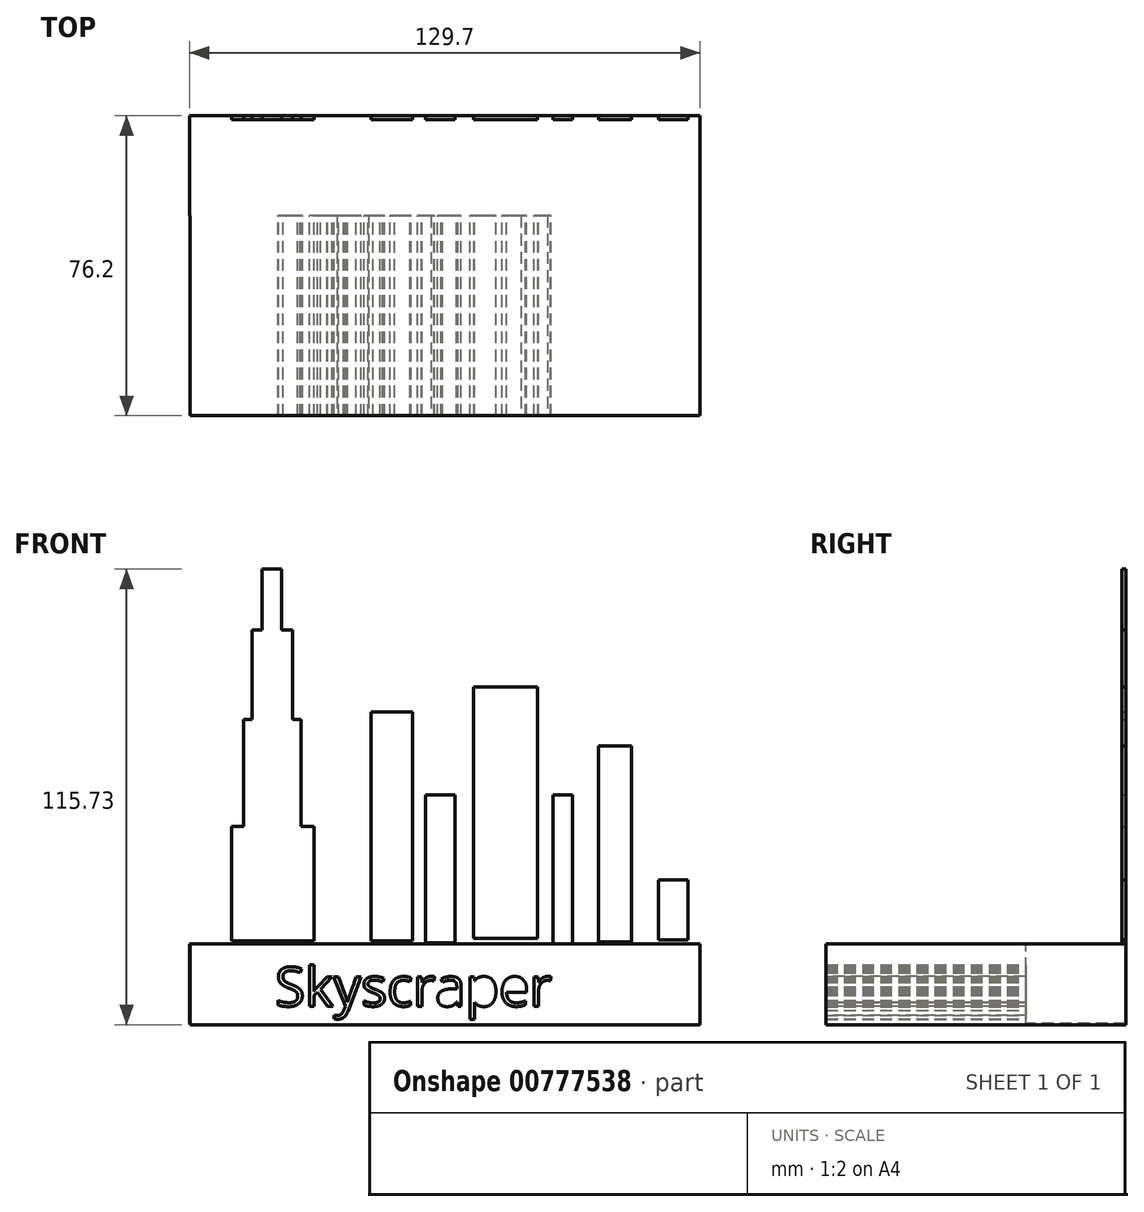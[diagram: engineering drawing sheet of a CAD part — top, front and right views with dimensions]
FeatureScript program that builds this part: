
annotation { "Feature Type Name" : "Feature", "Feature Type Description" : "" }
export const myFeature = defineFeature(function(context is Context, id is Id, definition is map)
    precondition{}
    {
        {
            var Q0;
            Q0=qCreatedBy(makeId("Front.planeOp"),FACE);
            var sketch = newSketch(context, id + "F0", { "sketchPlane" : qUnion([Q0])});
            skLineSegment(sketch, "E0.bottom", {"start": v(-62.22, -50.32) * mm, "end": v(67.34, -50.32) * mm});
            skLineSegment(sketch, "E0.top", {"start": v(-62.22, -29.83) * mm, "end": v(67.34, -29.83) * mm});
            skLineSegment(sketch, "E0.left", {"start": v(-62.22, -50.32) * mm, "end": v(-62.22, -29.83) * mm});
            skLineSegment(sketch, "E0.right", {"start": v(67.34, -50.32) * mm, "end": v(67.34, -29.83) * mm});
            skText(sketch, "E1", { "text": "Skyscraper", "fontName": "OpenSans-Regular.ttf"});
            const initialGuessF0  = {"E1": [-0.04063, -0.04561, 1, 0, 0.00997]};
            skSetInitialGuess(sketch, initialGuessF0);
            skSolve(sketch);
        }
        {
            var Q0;
            Q0=qCreatedBy(makeId("Front.planeOp"),FACE);
            var sketch = newSketch(context, id + "F1", { "sketchPlane" : qUnion([Q0])});
            skLineSegment(sketch, "E2.bottom", {"start": v(-51.7, -29) * mm, "end": v(-30.66, -29) * mm});
            skLineSegment(sketch, "E2.top", {"start": v(-51.7, 0) * mm, "end": v(-30.66, 0) * mm});
            skLineSegment(sketch, "E2.left", {"start": v(-51.7, -29) * mm, "end": v(-51.7, 0) * mm});
            skLineSegment(sketch, "E2.right", {"start": v(-30.66, -29) * mm, "end": v(-30.66, 0) * mm});
            skLineSegment(sketch, "E3.bottom", {"start": v(-48.66, 0) * mm, "end": v(-33.98, 0) * mm});
            skLineSegment(sketch, "E3.top", {"start": v(-48.66, 27.2) * mm, "end": v(-33.98, 27.2) * mm});
            skLineSegment(sketch, "E3.left", {"start": v(-48.66, 0) * mm, "end": v(-48.66, 27.2) * mm});
            skLineSegment(sketch, "E3.right", {"start": v(-33.98, 0) * mm, "end": v(-33.98, 27.2) * mm});
            skLineSegment(sketch, "E4.bottom", {"start": v(-46.44, 27.2) * mm, "end": v(-36.2, 27.2) * mm});
            skLineSegment(sketch, "E4.top", {"start": v(-46.44, 49.9) * mm, "end": v(-36.2, 49.9) * mm});
            skLineSegment(sketch, "E4.left", {"start": v(-46.44, 27.2) * mm, "end": v(-46.44, 49.9) * mm});
            skLineSegment(sketch, "E4.right", {"start": v(-36.2, 27.2) * mm, "end": v(-36.2, 49.9) * mm});
            skLineSegment(sketch, "E5.bottom", {"start": v(-43.95, 49.9) * mm, "end": v(-38.97, 49.9) * mm});
            skLineSegment(sketch, "E5.top", {"start": v(-43.95, 65.4) * mm, "end": v(-38.97, 65.4) * mm});
            skLineSegment(sketch, "E5.left", {"start": v(-43.95, 49.9) * mm, "end": v(-43.95, 65.4) * mm});
            skLineSegment(sketch, "E5.right", {"start": v(-38.97, 49.9) * mm, "end": v(-38.97, 65.4) * mm});
            skPoint(sketch, "E6.oppositeSnap0", {"position": v(-41.46, 65.4) * mm});
            skLineSegment(sketch, "E6.bottom", {"start": v(-41.46, 65.4) * mm, "end": v(-41.46, 65.4) * mm});
            skLineSegment(sketch, "E6.top", {"start": v(-41.46, 73.99) * mm, "end": v(-41.46, 73.99) * mm});
            skLineSegment(sketch, "E6.left", {"start": v(-41.46, 65.4) * mm, "end": v(-41.46, 73.99) * mm});
            skLineSegment(sketch, "E6.right", {"start": v(-41.46, 65.4) * mm, "end": v(-41.46, 73.99) * mm});
            skLineSegment(sketch, "E7.bottom", {"start": v(-16.27, -29) * mm, "end": v(-5.74, -29) * mm});
            skLineSegment(sketch, "E7.top", {"start": v(-16.27, 29.14) * mm, "end": v(-5.74, 29.14) * mm});
            skLineSegment(sketch, "E7.left", {"start": v(-16.27, -29) * mm, "end": v(-16.27, 29.14) * mm});
            skLineSegment(sketch, "E7.right", {"start": v(-5.74, -29) * mm, "end": v(-5.74, 29.14) * mm});
            skLineSegment(sketch, "E8.bottom", {"start": v(9.76, -28.45) * mm, "end": v(26.1, -28.45) * mm});
            skLineSegment(sketch, "E8.top", {"start": v(9.76, 35.5) * mm, "end": v(26.1, 35.5) * mm});
            skLineSegment(sketch, "E8.left", {"start": v(9.76, -28.45) * mm, "end": v(9.76, 35.5) * mm});
            skLineSegment(sketch, "E8.right", {"start": v(26.1, -28.45) * mm, "end": v(26.1, 35.5) * mm});
            skLineSegment(sketch, "E9.bottom", {"start": v(41.6, -29.28) * mm, "end": v(49.9, -29.28) * mm});
            skLineSegment(sketch, "E9.top", {"start": v(41.6, 20.56) * mm, "end": v(49.9, 20.56) * mm});
            skLineSegment(sketch, "E9.left", {"start": v(41.6, -29.28) * mm, "end": v(41.6, 20.56) * mm});
            skLineSegment(sketch, "E9.right", {"start": v(49.9, -29.28) * mm, "end": v(49.9, 20.56) * mm});
            skLineSegment(sketch, "E10.bottom", {"start": v(29.97, -29.83) * mm, "end": v(34.95, -29.83) * mm});
            skLineSegment(sketch, "E10.top", {"start": v(29.97, 8.1) * mm, "end": v(34.95, 8.1) * mm});
            skLineSegment(sketch, "E10.left", {"start": v(29.97, -29.83) * mm, "end": v(29.97, 8.1) * mm});
            skLineSegment(sketch, "E10.right", {"start": v(34.95, -29.83) * mm, "end": v(34.95, 8.1) * mm});
            skLineSegment(sketch, "E11.bottom", {"start": v(-2.42, -29.55) * mm, "end": v(5.05, -29.55) * mm});
            skLineSegment(sketch, "E11.top", {"start": v(-2.42, 8.1) * mm, "end": v(5.05, 8.1) * mm});
            skLineSegment(sketch, "E11.left", {"start": v(-2.42, -29.55) * mm, "end": v(-2.42, 8.1) * mm});
            skLineSegment(sketch, "E11.right", {"start": v(5.05, -29.55) * mm, "end": v(5.05, 8.1) * mm});
            skLineSegment(sketch, "E12.bottom", {"start": v(56.82, -28.72) * mm, "end": v(64.3, -28.72) * mm});
            skLineSegment(sketch, "E12.top", {"start": v(56.82, -13.5) * mm, "end": v(64.3, -13.5) * mm});
            skLineSegment(sketch, "E12.left", {"start": v(56.82, -28.72) * mm, "end": v(56.82, -13.5) * mm});
            skLineSegment(sketch, "E12.right", {"start": v(64.3, -28.72) * mm, "end": v(64.3, -13.5) * mm});
            skSolve(sketch);
        }
        {
            var Q0;
            Q0 = qSketchRegion(id + "F1", true);
            extrude(context, id + "F2", {"entities" : qUnion([Q0]), "depth" : mm, "offsetDistance" : 25.4 * mm});
        }
        {
            var Q0;
            Q0 = qSketchRegion(id + "F0", true);
            extrude(context, id + "F3", {"entities" : qUnion([Q0]), "operationType" : NewBodyOperationType.ADD, "depth" : 76.2 * mm, "offsetDistance" : 25.4 * mm});
        }
        {
            var Q0;
            Q0=qCreatedBy(makeId("Front.planeOp"),FACE);
            var sketch = newSketch(context, id + "F4", { "sketchPlane" : qUnion([Q0])});
            skLineSegment(sketch, "E13.bottom", {"start": v(67.2, -50.04) * mm, "end": v(-62.36, -50.04) * mm});
            skLineSegment(sketch, "E13.top", {"start": v(67.2, -29.83) * mm, "end": v(-62.36, -29.83) * mm});
            skLineSegment(sketch, "E13.left", {"start": v(67.2, -50.04) * mm, "end": v(67.2, -29.83) * mm});
            skLineSegment(sketch, "E13.right", {"start": v(-62.36, -50.04) * mm, "end": v(-62.36, -29.83) * mm});
            skSolve(sketch);
        }
        {
            var Q0;
            Q0 = qSketchRegion(id + "F4", true);
            extrude(context, id + "F5", {"entities" : qUnion([Q0]), "operationType" : NewBodyOperationType.ADD, "depth" : 25.4 * mm, "offsetDistance" : 25.4 * mm});
        }
    });
